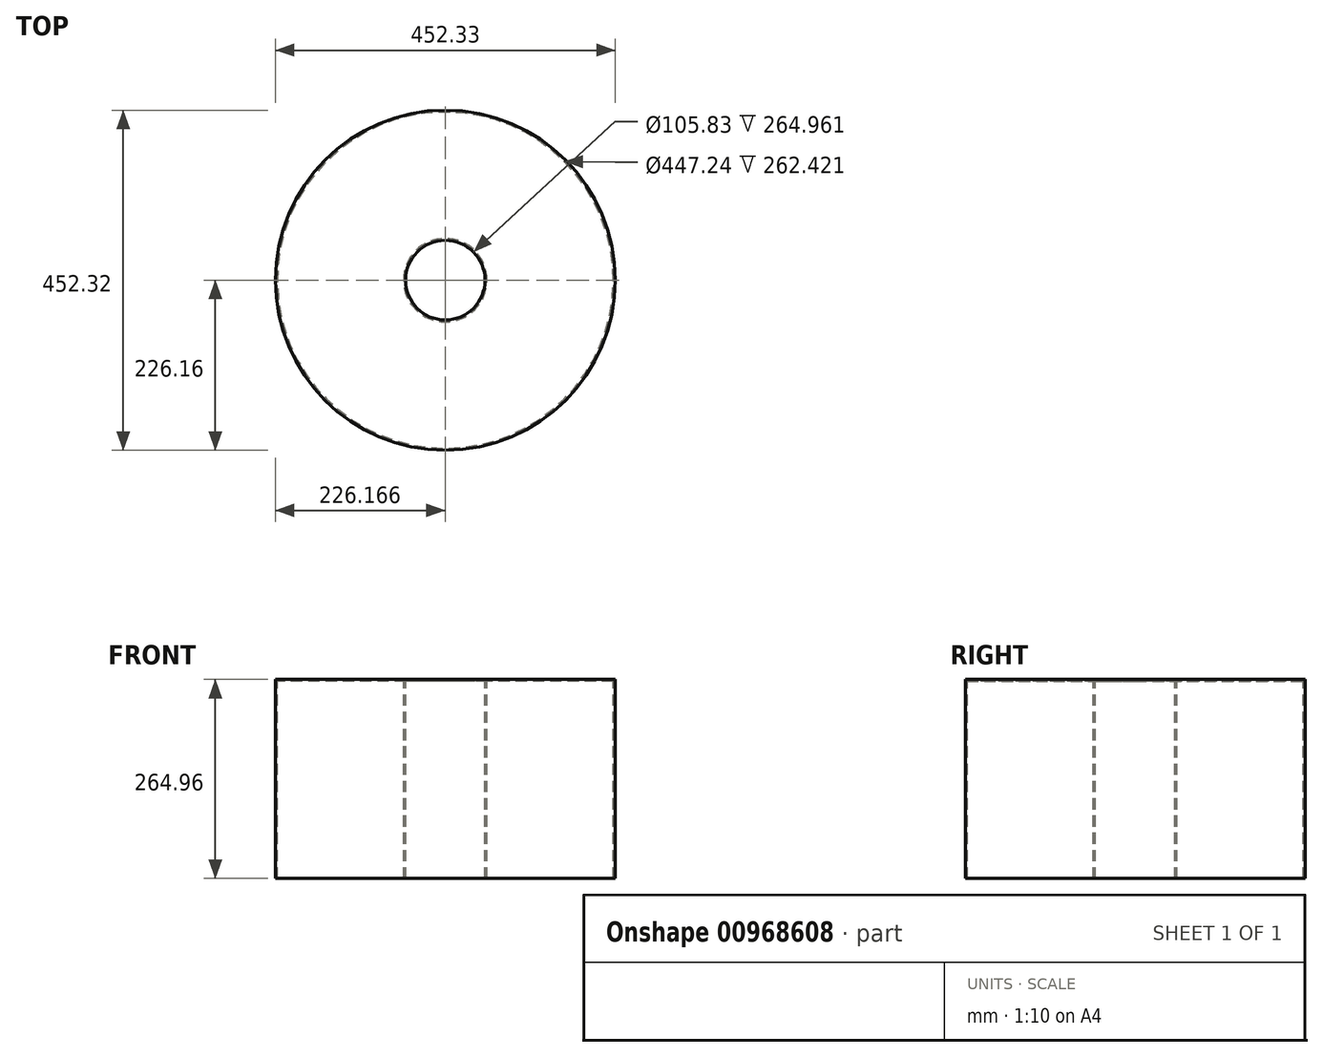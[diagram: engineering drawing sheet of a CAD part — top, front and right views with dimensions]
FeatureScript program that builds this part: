
annotation { "Feature Type Name" : "Feature", "Feature Type Description" : "" }
export const myFeature = defineFeature(function(context is Context, id is Id, definition is map)
    precondition{}
    {
        {
            var Q0;
            Q0=qCreatedBy(makeId("Front.planeOp"),FACE);
            var sketch = newSketch(context, id + "F0", { "sketchPlane" : qUnion([Q0])});
            skLineSegment(sketch, "E0.bottom", {"start": v(50.35, 0) * mm, "end": v(-122.9, 0) * mm});
            skLineSegment(sketch, "E0.top", {"start": v(50.35, 264.96) * mm, "end": v(-122.9, 264.96) * mm});
            skLineSegment(sketch, "E0.left", {"start": v(50.35, 0) * mm, "end": v(50.35, 264.96) * mm});
            skLineSegment(sketch, "E0.right", {"start": v(-122.9, 0) * mm, "end": v(-122.9, 264.96) * mm});
            skPoint(sketch, "E0.middle", {"position": v(-36.27, 132.48) * mm});
            skSolve(sketch);
        }
        {
            var Q0;
            Q0=qCreatedBy(makeId("Front.planeOp"),FACE);
            var sketch = newSketch(context, id + "F1", { "sketchPlane" : qUnion([Q0])});
            skLineSegment(sketch, "E1", {"start": v(103.27, 215.43) * mm, "end": v(103.27, 20.75) * mm});
            skSolve(sketch);
        }
        {
            var Q0;
            Q0=makeQuery(id+"F0.imprint","IMPRINT",FACE,{"disambiguationData":[TD([[makeQuery(id+"F0.imprint","IMPRINT",EDGE,{"derivedFrom":sQuery(id+"F0.wireOp",EDGE,"E0.bottom")}),-1.0]])]});
            var Q1;
            Q1=sQuery(id+"F1.wireOp",EDGE,"E1");
            revolve(context, id + "F2", {"surfaceOperationType" : NewSurfaceOperationType.NEW, "entities" : qUnion([Q0]), "axis" : qUnion([Q1]), "revolveType" : RevolveType.FULL});
        }
        {
            var Q0;
            Q0=makeQuery(id+"F2.opRevolve","SWEPT_FACE",FACE,{"disambiguationData":[OSD([sQuery(id+"F0.wireOp",EDGE,"E0.bottom")])]});
            shell(context, id + "F3", {"entities" : qUnion([Q0]), "thickness" : 2.54 * mm});
        }
    });
